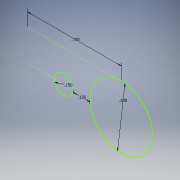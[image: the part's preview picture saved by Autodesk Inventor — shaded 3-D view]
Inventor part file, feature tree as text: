
AUTODESK INVENTOR PART (.ipt)
format: ipt  version: 2016 (Build 200138000, 138)  size: 84,992 bytes
history: native  units: in
note: dims shown in document units (in); Inventor stores cm internally (conversion verified against a paired STEP export)
features: sketch x1
ambient origin geometry x8: Origin, YZ Plane, XZ Plane, XY Plane, X Axis, Y Axis, Z Axis, Center Point
feature tree (1):
  sketch  "Sketch1"  dims[d7=0.5in d8=0.75in d11=0.135in d12=0.15in]
